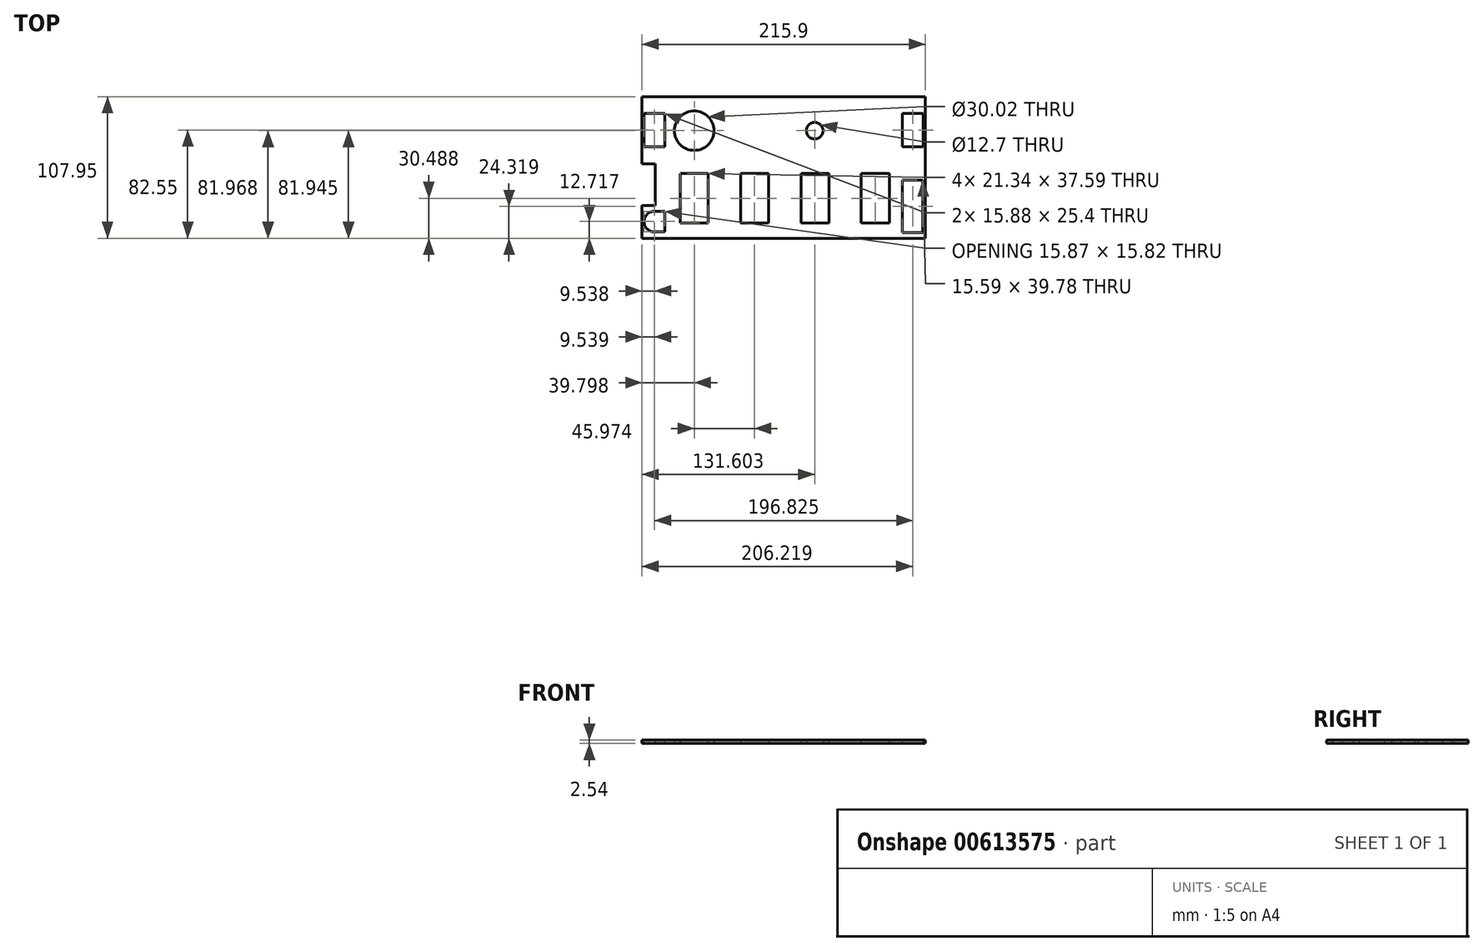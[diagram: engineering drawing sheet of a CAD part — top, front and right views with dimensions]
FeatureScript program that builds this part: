
annotation { "Feature Type Name" : "Feature", "Feature Type Description" : "" }
export const myFeature = defineFeature(function(context is Context, id is Id, definition is map)
    precondition{}
    {
        {
            var Q0;
            Q0=qCreatedBy(makeId("Top.planeOp"),FACE);
            var sketch = newSketch(context, id + "F0", { "sketchPlane" : qUnion([Q0])});
            skLineSegment(sketch, "E0.bottom", {"start": v(0, 0) * mm, "end": v(215.9, 0) * mm});
            skLineSegment(sketch, "E0.top", {"start": v(0, -107.95) * mm, "end": v(215.9, -107.95) * mm});
            skLineSegment(sketch, "E0.left", {"start": v(0, 0) * mm, "end": v(0, -107.95) * mm});
            skLineSegment(sketch, "E0.right", {"start": v(215.9, 0) * mm, "end": v(215.9, -107.95) * mm});
            skSolve(sketch);
        }
        {
            var Q0;
            Q0 = qSketchRegion(id + "F0", true);
            extrude(context, id + "F1", {"entities" : qUnion([Q0]), "depth" : 2.54 * mm, "offsetDistance" : 25.4 * mm});
        }
        {
            var Q0;
            Q0=makeQuery(id+"F0.imprint","IMPRINT",FACE,{"disambiguationData":[TD([[makeQuery(id+"F0.imprint","IMPRINT",EDGE,{"derivedFrom":sQuery(id+"F0.wireOp",EDGE,"E0.bottom")}),-1.0]])]});
            var sketch = newSketch(context, id + "F2", { "sketchPlane" : qUnion([Q0])});
            skCircle(sketch, "E1", {"center": v(39.8, -26) * mm, "radius": 15.01 * mm});
            skLineSegment(sketch, "E2.bottom", {"start": v(29.13, -58.67) * mm, "end": v(50.47, -58.67) * mm});
            skLineSegment(sketch, "E2.top", {"start": v(29.13, -96.26) * mm, "end": v(50.47, -96.26) * mm});
            skLineSegment(sketch, "E2.left", {"start": v(29.13, -58.67) * mm, "end": v(29.13, -96.26) * mm});
            skLineSegment(sketch, "E2.right", {"start": v(50.47, -58.67) * mm, "end": v(50.47, -96.26) * mm});
            skLineSegment(sketch, "E3.1.0.0", {"start": v(75.1, -58.67) * mm, "end": v(96.44, -58.67) * mm});
            skLineSegment(sketch, "E3.1.0.1", {"start": v(75.1, -58.67) * mm, "end": v(75.1, -96.26) * mm});
            skLineSegment(sketch, "E3.1.0.2", {"start": v(96.44, -58.67) * mm, "end": v(96.44, -96.26) * mm});
            skLineSegment(sketch, "E3.1.0.3", {"start": v(75.1, -96.26) * mm, "end": v(96.44, -96.26) * mm});
            skLineSegment(sketch, "E3.2.0.0", {"start": v(121.08, -58.67) * mm, "end": v(142.41, -58.67) * mm});
            skLineSegment(sketch, "E3.2.0.1", {"start": v(121.08, -58.67) * mm, "end": v(121.08, -96.26) * mm});
            skLineSegment(sketch, "E3.2.0.2", {"start": v(142.41, -58.67) * mm, "end": v(142.41, -96.26) * mm});
            skLineSegment(sketch, "E3.2.0.3", {"start": v(121.08, -96.26) * mm, "end": v(142.41, -96.26) * mm});
            skLineSegment(sketch, "E3.3.0.0", {"start": v(167.05, -58.67) * mm, "end": v(188.39, -58.67) * mm});
            skLineSegment(sketch, "E3.3.0.1", {"start": v(167.05, -58.67) * mm, "end": v(167.05, -96.26) * mm});
            skLineSegment(sketch, "E3.3.0.2", {"start": v(188.39, -58.67) * mm, "end": v(188.39, -96.26) * mm});
            skLineSegment(sketch, "E3.3.0.3", {"start": v(167.05, -96.26) * mm, "end": v(188.39, -96.26) * mm});
            skLineSegment(sketch, "E3.direction1", {"start": v(29.13, -96.26) * mm, "end": v(75.1, -96.26) * mm, "construction": true});
            skPoint(sketch, "E4", {"position": v(39.8, -58.67) * mm});
            skCircle(sketch, "E5", {"center": v(131.6, -25.98) * mm, "radius": 6.35 * mm});
            skSolve(sketch);
        }
        {
            var Q0;
            Q0 = qSketchRegion(id + "F2", true);
            extrude(context, id + "F3", {"entities" : qUnion([Q0]), "operationType" : NewBodyOperationType.REMOVE, "depth" : 25.4 * mm, "offsetDistance" : 25.4 * mm});
        }
        {
            var Q0;
            Q0=makeQuery(id+"F1.opExtrude","CAP_FACE",FACE,{"disambiguationData":[OSD([sQuery(id+"F0.wireOp",EDGE,"E0.bottom"),sQuery(id+"F0.wireOp",EDGE,"E0.top"),sQuery(id+"F0.wireOp",EDGE,"E0.left"),sQuery(id+"F0.wireOp",EDGE,"E0.right")])],"isStart":false});
            var sketch = newSketch(context, id + "F4", { "sketchPlane" : qUnion([Q0])});
            skLineSegment(sketch, "E6.bottom", {"start": v(1.6, -12.7) * mm, "end": v(17.48, -12.7) * mm});
            skLineSegment(sketch, "E6.top", {"start": v(1.6, -38.1) * mm, "end": v(17.48, -38.1) * mm});
            skLineSegment(sketch, "E6.left", {"start": v(1.6, -12.7) * mm, "end": v(1.6, -38.1) * mm});
            skLineSegment(sketch, "E6.right", {"start": v(17.48, -12.7) * mm, "end": v(17.48, -38.1) * mm});
            skArc(sketch, "E7", {"start": v(9.95, -87.32) * mm, "mid": v(1.6, -95.46) * mm, "end": v(10.38, -103.14) * mm});
            skPoint(sketch, "E7.centerSnap0", {"position": v(9.54, -38.1) * mm});
            skLineSegment(sketch, "E8", {"start": v(17.48, -87.32) * mm, "end": v(17.48, -103.14) * mm});
            skLineSegment(sketch, "E9", {"start": v(10.38, -103.14) * mm, "end": v(17.48, -103.14) * mm});
            skLineSegment(sketch, "E10", {"start": v(9.95, -87.32) * mm, "end": v(17.48, -87.32) * mm});
            skPoint(sketch, "E11.orphan", {"position": v(17.48, -76.63) * mm});
            skPoint(sketch, "E12.orphan", {"position": v(17.48, -95.68) * mm});
            skLineSegment(sketch, "E13.MirrorCS", {"start": v(214.3, -38.1) * mm, "end": v(198.42, -38.1) * mm});
            skLineSegment(sketch, "E14.MirrorCS", {"start": v(198.42, -12.7) * mm, "end": v(198.42, -38.1) * mm});
            skLineSegment(sketch, "E15.MirrorCS", {"start": v(214.3, -12.7) * mm, "end": v(214.3, -38.1) * mm});
            skLineSegment(sketch, "E16.MirrorCS", {"start": v(214.3, -12.7) * mm, "end": v(198.42, -12.7) * mm});
            skLineSegment(sketch, "E17.top", {"start": v(198.42, -63.74) * mm, "end": v(214.01, -63.74) * mm});
            skLineSegment(sketch, "E18.top", {"start": v(198.42, -103.52) * mm, "end": v(214.01, -103.52) * mm});
            skLineSegment(sketch, "E18.left", {"start": v(198.42, -63.74) * mm, "end": v(198.42, -103.52) * mm});
            skLineSegment(sketch, "E18.right", {"start": v(214.01, -63.74) * mm, "end": v(214.01, -103.52) * mm});
            skSolve(sketch);
        }
        {
            var Q0;
            Q0 = qSketchRegion(id + "F4", true);
            extrude(context, id + "F5", {"entities" : qUnion([Q0]), "operationType" : NewBodyOperationType.REMOVE, "oppositeDirection" : true, "depth" : 25.4 * mm, "offsetDistance" : 25.4 * mm});
        }
        {
            var Q0;
            Q0=makeQuery(id+"F1.opExtrude","CAP_FACE",FACE,{"disambiguationData":[OSD([sQuery(id+"F0.wireOp",EDGE,"E0.bottom"),sQuery(id+"F0.wireOp",EDGE,"E0.top"),sQuery(id+"F0.wireOp",EDGE,"E0.left"),sQuery(id+"F0.wireOp",EDGE,"E0.right")])],"isStart":false});
            var sketch = newSketch(context, id + "F6", { "sketchPlane" : qUnion([Q0])});
            skLineSegment(sketch, "E19.bottom", {"start": v(0, -51.2) * mm, "end": v(9.95, -51.2) * mm});
            skLineSegment(sketch, "E19.top", {"start": v(0, -82.95) * mm, "end": v(9.95, -82.95) * mm});
            skLineSegment(sketch, "E19.left", {"start": v(0, -51.2) * mm, "end": v(0, -82.95) * mm});
            skLineSegment(sketch, "E19.right", {"start": v(9.95, -51.2) * mm, "end": v(9.95, -82.95) * mm});
            skSolve(sketch);
        }
        {
            var Q0;
            Q0=makeQuery(id+"F6.imprint","IMPRINT",FACE,{"disambiguationData":[TD([[makeQuery(id+"F6.imprint","IMPRINT",EDGE,{"derivedFrom":sQuery(id+"F6.wireOp",EDGE,"E19.bottom")}),-1.0]])]});
            extrude(context, id + "F7", {"entities" : qUnion([Q0]), "operationType" : NewBodyOperationType.REMOVE, "oppositeDirection" : true, "depth" : 25.4 * mm, "offsetDistance" : 25.4 * mm});
        }
    });
